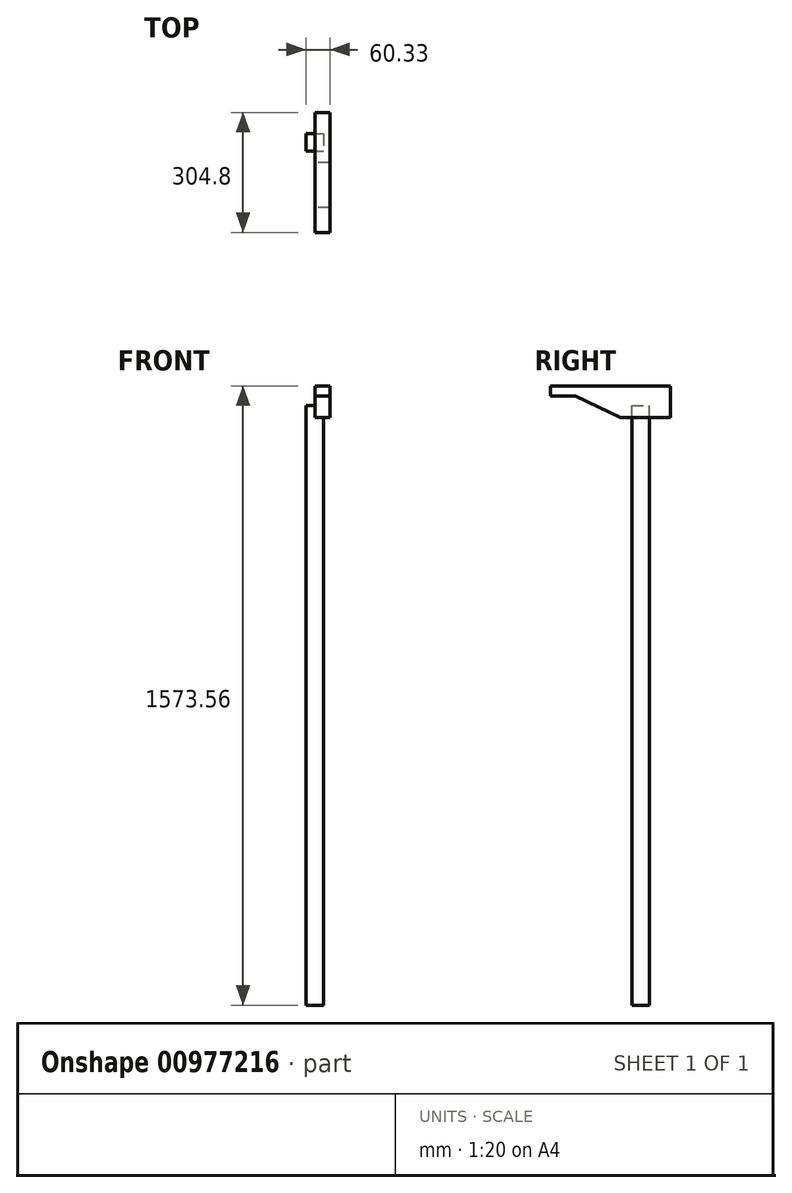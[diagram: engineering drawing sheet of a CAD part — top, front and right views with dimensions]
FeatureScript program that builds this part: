
annotation { "Feature Type Name" : "Feature", "Feature Type Description" : "" }
export const myFeature = defineFeature(function(context is Context, id is Id, definition is map)
    precondition{}
    {
        {
            var Q0;
            Q0=qCreatedBy(makeId("Top.planeOp"),FACE);
            var sketch = newSketch(context, id + "F0", { "sketchPlane" : qUnion([Q0])});
            skLineSegment(sketch, "E0.bottom", {"start": v(-22.23, 22.23) * mm, "end": v(22.23, 22.23) * mm});
            skLineSegment(sketch, "E0.top", {"start": v(-22.23, -22.22) * mm, "end": v(22.23, -22.22) * mm});
            skLineSegment(sketch, "E0.left", {"start": v(-22.23, 22.23) * mm, "end": v(-22.22, -22.23) * mm});
            skLineSegment(sketch, "E0.right", {"start": v(22.23, 22.23) * mm, "end": v(22.23, -22.22) * mm});
            skSolve(sketch);
        }
        {
            var Q0;
            Q0 = qSketchRegion(id + "F0", true);
            extrude(context, id + "F1", {"entities" : qUnion([Q0]), "oppositeDirection" : true, "depth" : 1524 * mm, "offsetDistance" : 25.4 * mm});
        }
        {
            var Q0;
            Q0=qCreatedBy(makeId("Right.planeOp"),FACE);
            var sketch = newSketch(context, id + "F2", { "sketchPlane" : qUnion([Q0])});
            skLineSegment(sketch, "E1", {"start": v(76.36, 49.56) * mm, "end": v(-228.44, 49.56) * mm});
            skLineSegment(sketch, "E2", {"start": v(76.36, 49.56) * mm, "end": v(76.36, -31.2) * mm});
            skLineSegment(sketch, "E3", {"start": v(76.36, -31.2) * mm, "end": v(-50.64, -31.2) * mm});
            skLineSegment(sketch, "E4", {"start": v(-50.64, -31.2) * mm, "end": v(-164.94, 24.16) * mm});
            skLineSegment(sketch, "E5", {"start": v(-164.94, 24.16) * mm, "end": v(-228.44, 24.16) * mm});
            skLineSegment(sketch, "E6", {"start": v(-228.44, 24.16) * mm, "end": v(-228.44, 49.56) * mm});
            skSolve(sketch);
        }
        {
            var Q0;
            Q0 = qSketchRegion(id + "F2", true);
            extrude(context, id + "F3", {"entities" : qUnion([Q0]), "operationType" : NewBodyOperationType.ADD, "depth" : 38.1 * mm, "offsetDistance" : 25.4 * mm});
        }
    });
